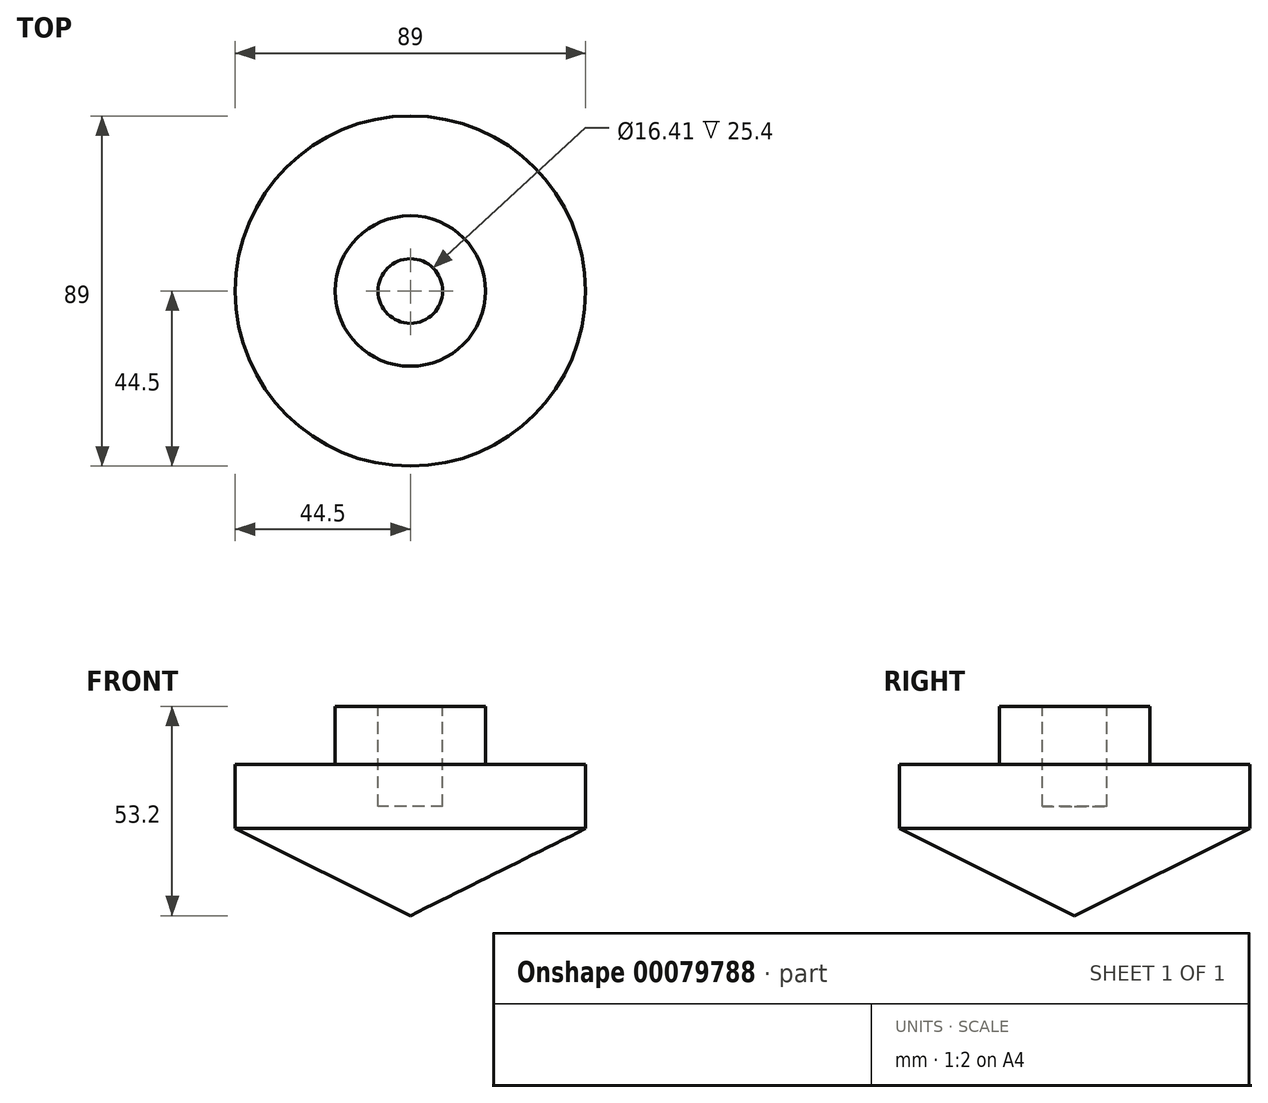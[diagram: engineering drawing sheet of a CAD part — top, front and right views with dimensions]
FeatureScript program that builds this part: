
annotation { "Feature Type Name" : "Feature", "Feature Type Description" : "" }
export const myFeature = defineFeature(function(context is Context, id is Id, definition is map)
    precondition{}
    {
        {
            var Q0;
            Q0=qCreatedBy(makeId("Front.planeOp"),FACE);
            var sketch = newSketch(context, id + "F0", { "sketchPlane" : qUnion([Q0])});
            skLineSegment(sketch, "E0", {"start": v(0, 0) * mm, "end": v(44.5, 22.1) * mm});
            skLineSegment(sketch, "E1", {"start": v(44.5, 22.1) * mm, "end": v(44.5, 38.36) * mm});
            skLineSegment(sketch, "E2", {"start": v(44.5, 38.36) * mm, "end": v(19.11, 38.36) * mm});
            skLineSegment(sketch, "E3", {"start": v(19.11, 38.36) * mm, "end": v(19.11, 53.2) * mm});
            skLineSegment(sketch, "E4", {"start": v(19.11, 53.2) * mm, "end": v(0, 53.2) * mm});
            skLineSegment(sketch, "E5", {"start": v(0, 53.2) * mm, "end": v(0, 0) * mm});
            skSolve(sketch);
        }
        {
            var Q0;
            Q0 = qSketchRegion(id + "F0", true);
            var Q1;
            Q1=sQuery(id+"F0.wireOp",EDGE,"E5");
            revolve(context, id + "F1", {"entities" : qUnion([Q0]), "axis" : qUnion([Q1]), "revolveType" : RevolveType.FULL});
        }
        {
            var Q0;
            Q0=makeQuery(id+"F1.opRevolve","SWEPT_FACE",FACE,{"disambiguationData":[OSD([sQuery(id+"F0.wireOp",EDGE,"E4")])]});
            var sketch = newSketch(context, id + "F2", { "sketchPlane" : qUnion([Q0])});
            skCircle(sketch, "E6", {"center": v(0, 0) * mm, "radius": 8.2 * mm});
            skSolve(sketch);
        }
        {
            var Q0;
            Q0=makeQuery(id+"F2.imprint","IMPRINT",FACE,{"disambiguationData":[TD([[makeQuery(id+"F2.imprint","IMPRINT",EDGE,{"derivedFrom":sQuery(id+"F2.wireOp",EDGE,"E6")}),1.0]])]});
            extrude(context, id + "F3", {"entities" : qUnion([Q0]), "operationType" : NewBodyOperationType.REMOVE, "oppositeDirection" : true, "depth" : 25.4 * mm});
        }
    });
